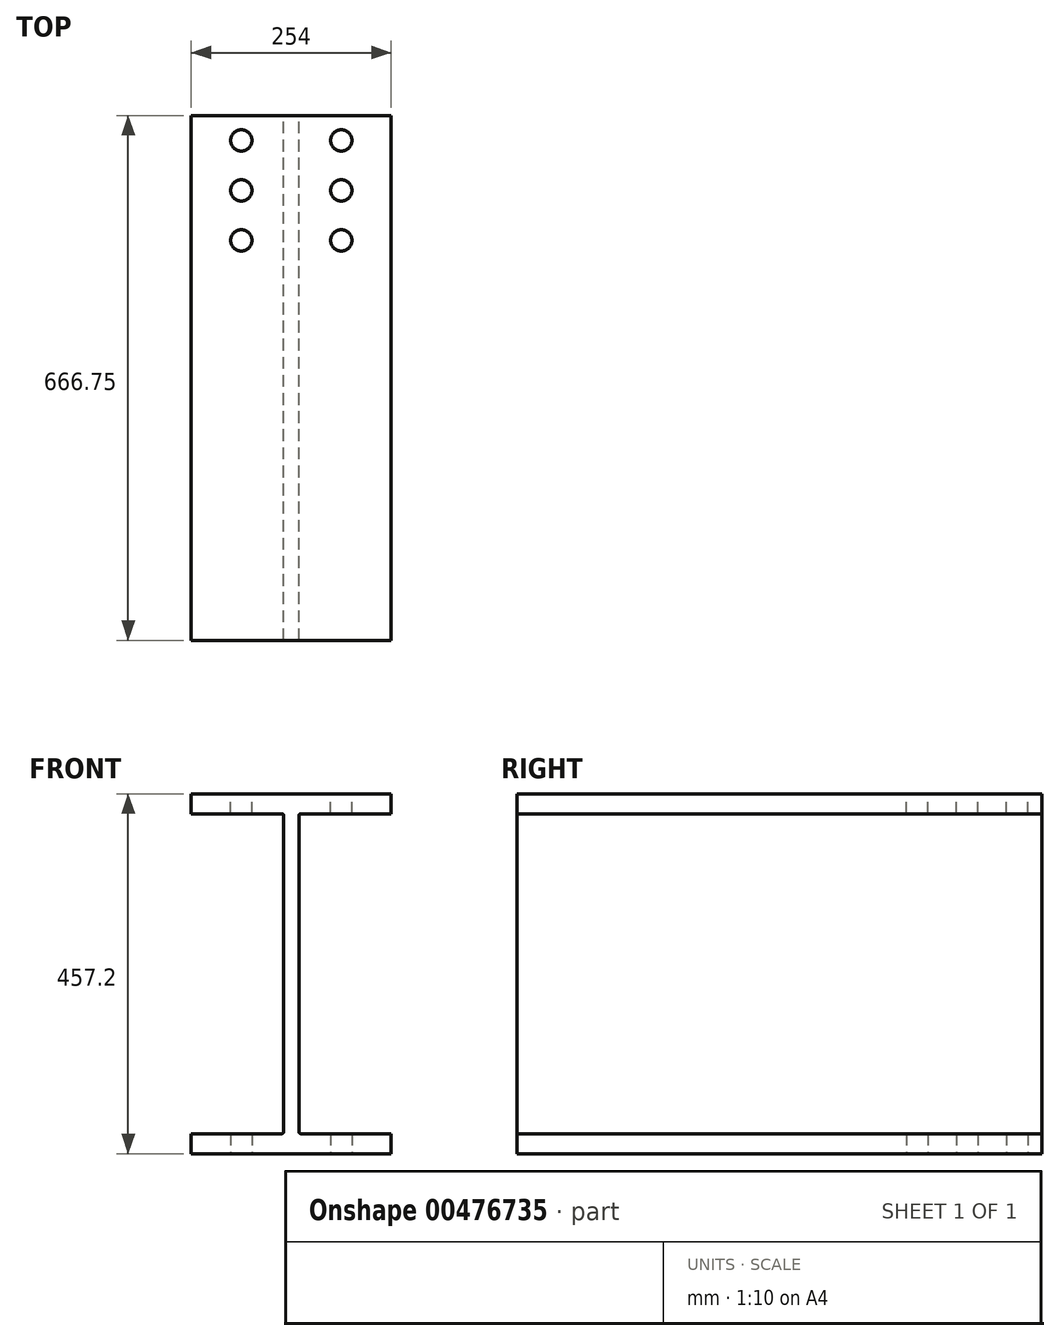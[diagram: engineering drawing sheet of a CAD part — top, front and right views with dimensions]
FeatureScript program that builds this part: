
annotation { "Feature Type Name" : "Feature", "Feature Type Description" : "" }
export const myFeature = defineFeature(function(context is Context, id is Id, definition is map)
    precondition{}
    {
        {
            var Q0;
            Q0=qCreatedBy(makeId("Front.planeOp"),FACE);
            var sketch = newSketch(context, id + "F0", { "sketchPlane" : qUnion([Q0])});
            skLineSegment(sketch, "E0", {"start": v(127, -203.2) * mm, "end": v(12.06, -203.2) * mm});
            skLineSegment(sketch, "E1", {"start": v(9.52, -200.66) * mm, "end": v(9.52, 200.66) * mm});
            skLineSegment(sketch, "E2", {"start": v(12.06, 203.2) * mm, "end": v(127, 203.2) * mm});
            skLineSegment(sketch, "E3", {"start": v(-127, 203.2) * mm, "end": v(-12.06, 203.2) * mm});
            skLineSegment(sketch, "E4", {"start": v(-9.53, 200.66) * mm, "end": v(-9.53, -200.66) * mm});
            skLineSegment(sketch, "E5", {"start": v(-12.06, -203.2) * mm, "end": v(-127, -203.2) * mm});
            skLineSegment(sketch, "E6", {"start": v(0, 0) * mm, "end": v(-9.52, 0) * mm, "construction": true});
            skLineSegment(sketch, "E7", {"start": v(0, 0) * mm, "end": v(9.52, 0) * mm, "construction": true});
            skLineSegment(sketch, "E8", {"start": v(0, 0) * mm, "end": v(0, 228.6) * mm, "construction": true});
            skLineSegment(sketch, "E9", {"start": v(0, 0) * mm, "end": v(0, -228.6) * mm, "construction": true});
            skPoint(sketch, "E10.visualSharp", {"position": v(-9.53, 203.2) * mm});
            skArc(sketch, "E10.filletArc", {"start": v(-9.52, 200.66) * mm, "mid": v(-10.27, 202.46) * mm, "end": v(-12.06, 203.2) * mm});
            skPoint(sketch, "E11.visualSharp", {"position": v(9.53, 203.2) * mm});
            skArc(sketch, "E11.filletArc", {"start": v(12.06, 203.2) * mm, "mid": v(10.27, 202.46) * mm, "end": v(9.52, 200.66) * mm});
            skPoint(sketch, "E12.visualSharp", {"position": v(9.53, -203.2) * mm});
            skArc(sketch, "E12.filletArc", {"start": v(9.52, -200.66) * mm, "mid": v(10.27, -202.46) * mm, "end": v(12.06, -203.2) * mm});
            skPoint(sketch, "E13.visualSharp", {"position": v(-9.53, -203.2) * mm});
            skArc(sketch, "E13.filletArc", {"start": v(-12.06, -203.2) * mm, "mid": v(-10.27, -202.46) * mm, "end": v(-9.52, -200.66) * mm});
            skPoint(sketch, "E14.visualSharp", {"position": v(-127, 228.6) * mm});
            skPoint(sketch, "E15.visualSharp", {"position": v(127, 228.6) * mm});
            skPoint(sketch, "E16.visualSharp", {"position": v(127, 203.2) * mm});
            skPoint(sketch, "E17.visualSharp", {"position": v(127, -228.6) * mm});
            skPoint(sketch, "E18.visualSharp", {"position": v(-127, -203.2) * mm});
            skPoint(sketch, "E19.visualSharp", {"position": v(-127, -228.6) * mm});
            skLineSegment(sketch, "E20", {"start": v(127, -203.2) * mm, "end": v(127, -228.6) * mm});
            skLineSegment(sketch, "E21", {"start": v(-127, -203.2) * mm, "end": v(-127, -228.6) * mm});
            skLineSegment(sketch, "E22", {"start": v(-127, 228.6) * mm, "end": v(-127, 203.2) * mm});
            skLineSegment(sketch, "E23", {"start": v(127, 228.6) * mm, "end": v(127, 203.2) * mm});
            skLineSegment(sketch, "E24", {"start": v(-127, 228.6) * mm, "end": v(127, 228.6) * mm});
            skLineSegment(sketch, "E25", {"start": v(-127, -228.6) * mm, "end": v(127, -228.6) * mm});
            skSolve(sketch);
        }
        {
            var Q0;
            Q0=makeQuery(id+"F0.imprint","IMPRINT",FACE,{"disambiguationData":[TD([[makeQuery(id+"F0.imprint","IMPRINT",EDGE,{"derivedFrom":sQuery(id+"F0.wireOp",EDGE,"E0")}),1.0]])]});
            extrude(context, id + "F1", {"entities" : qUnion([Q0]), "depth" : 508 * mm, "hasSecondDirection" : true, "secondDirectionOppositeDirection" : true, "secondDirectionDepth" : 158.75 * mm});
        }
        {
            var Q0;
            Q0=makeQuery(id+"F1.opExtrude","SWEPT_FACE",FACE,{"disambiguationData":[OSD([sQuery(id+"F0.wireOp",EDGE,"E24")])]});
            var sketch = newSketch(context, id + "F2", { "sketchPlane" : qUnion([Q0])});
            skLineSegment(sketch, "E26", {"start": v(0, 470.86) * mm, "end": v(0, -382.8) * mm, "construction": true});
            skPoint(sketch, "E27", {"position": v(63.5, 127) * mm});
            skPoint(sketch, "E28.0.1.0", {"position": v(63.5, 63.5) * mm});
            skPoint(sketch, "E28.0.2.0", {"position": v(63.5, 0) * mm});
            skLineSegment(sketch, "E28.direction1", {"start": v(63.5, 127) * mm, "end": v(88.9, 127) * mm, "construction": true});
            skLineSegment(sketch, "E28.direction2", {"start": v(63.5, 127) * mm, "end": v(63.5, 63.5) * mm, "construction": true});
            skPoint(sketch, "E29.MirrorP", {"position": v(-63.5, 0) * mm});
            skLineSegment(sketch, "E30.MirrorCS", {"start": v(-63.5, 127) * mm, "end": v(-63.5, 63.5) * mm, "construction": true});
            skPoint(sketch, "E31.MirrorP", {"position": v(-63.5, 127) * mm});
            skPoint(sketch, "E32.MirrorP", {"position": v(-63.5, 63.5) * mm});
            skSolve(sketch);
        }
        {
            var Q0;
            Q0=sQuery(id+"F2.wireOp",VERTEX,"E27");
            var Q1;
            Q1=sQuery(id+"F2.wireOp",VERTEX,"E28.0.1.0");
            var Q2;
            Q2=sQuery(id+"F2.wireOp",VERTEX,"E28.0.2.0");
            var Q3;
            Q3=sQuery(id+"F2.wireOp",VERTEX,"E28.0.3.0");
            var Q4;
            Q4=sQuery(id+"F2.wireOp",VERTEX,"E28.0.4.0");
            var Q5;
            Q5=sQuery(id+"F2.wireOp",VERTEX,"E28.0.5.0");
            var Q6;
            Q6=sQuery(id+"F2.wireOp",VERTEX,"10dad2e2-d4e5-4773-874c-b5d4de7557793.MirrorP");
            var Q7;
            Q7=sQuery(id+"F2.wireOp",VERTEX,"10dad2e2-d4e5-4773-874c-b5d4de7557794.MirrorP");
            var Q8;
            Q8=sQuery(id+"F2.wireOp",VERTEX,"10dad2e2-d4e5-4773-874c-b5d4de7557795.MirrorP");
            var Q9;
            Q9=sQuery(id+"F2.wireOp",VERTEX,"E29.MirrorP");
            var Q10;
            Q10=sQuery(id+"F2.wireOp",VERTEX,"E30.MirrorCS.end");
            var Q11;
            Q11=sQuery(id+"F2.wireOp",VERTEX,"E31.MirrorP");
            var Q12;
            Q12=makeQuery(id+"F1.opExtrude","SWEPT_BODY",BODY,{"disambiguationData":[OSD([sQuery(id+"F0.wireOp",EDGE,"E0"),sQuery(id+"F0.wireOp",EDGE,"E1"),sQuery(id+"F0.wireOp",EDGE,"E2"),sQuery(id+"F0.wireOp",EDGE,"E3"),sQuery(id+"F0.wireOp",EDGE,"E4"),sQuery(id+"F0.wireOp",EDGE,"E5"),sQuery(id+"F0.wireOp",EDGE,"E10.filletArc"),sQuery(id+"F0.wireOp",EDGE,"E11.filletArc"),sQuery(id+"F0.wireOp",EDGE,"E12.filletArc"),sQuery(id+"F0.wireOp",EDGE,"E13.filletArc"),sQuery(id+"F0.wireOp",EDGE,"E20"),sQuery(id+"F0.wireOp",EDGE,"E21"),sQuery(id+"F0.wireOp",EDGE,"E22"),sQuery(id+"F0.wireOp",EDGE,"E23"),sQuery(id+"F0.wireOp",EDGE,"E24"),sQuery(id+"F0.wireOp",EDGE,"E25")])]});
            hole(context, id + "F3", {"style" : HoleStyle.SIMPLE, "endStyle" : HoleEndStyle.BLIND, "holeDiameter" : 26.99 * mm, "holeDepth" : 25.4 * mm, "isTappedThrough" : true, "tappedDepth" : 12.7 * mm, "tapClearance" : 3, "locations" : qUnion([Q0, Q1, Q2, Q3, Q4, Q5, Q6, Q7, Q8, Q9, Q10, Q11]), "scope" : qUnion([Q12])});
        }
        {
            var Q0;
            Q0=makeQuery(id+"F1.opExtrude","SWEPT_FACE",FACE,{"disambiguationData":[OSD([sQuery(id+"F0.wireOp",EDGE,"E25")])]});
            var sketch = newSketch(context, id + "F4", { "sketchPlane" : qUnion([Q0])});
            skLineSegment(sketch, "E33", {"start": v(0, 396.6) * mm, "end": v(0, -457.05) * mm, "construction": true});
            skPoint(sketch, "E34", {"position": v(63.5, 0) * mm});
            skPoint(sketch, "E35.0.1.0", {"position": v(63.5, -63.5) * mm});
            skPoint(sketch, "E35.0.2.0", {"position": v(63.5, -127) * mm});
            skLineSegment(sketch, "E35.direction1", {"start": v(63.5, 0) * mm, "end": v(88.9, 0) * mm, "construction": true});
            skLineSegment(sketch, "E35.direction2", {"start": v(63.5, 0) * mm, "end": v(63.5, -63.5) * mm, "construction": true});
            skPoint(sketch, "E36.MirrorP", {"position": v(-63.5, -127) * mm});
            skLineSegment(sketch, "E37.MirrorCS", {"start": v(-63.5, 0) * mm, "end": v(-63.5, -63.5) * mm, "construction": true});
            skPoint(sketch, "E38.MirrorP", {"position": v(-63.5, 0) * mm});
            skPoint(sketch, "E39.MirrorP", {"position": v(-63.5, -63.5) * mm});
            skSolve(sketch);
        }
        {
            var Q0;
            Q0=sQuery(id+"F4.wireOp",VERTEX,"E35.0.2.0");
            var Q1;
            Q1=sQuery(id+"F4.wireOp",VERTEX,"E35.0.1.0");
            var Q2;
            Q2=sQuery(id+"F4.wireOp",VERTEX,"E34");
            var Q3;
            Q3=sQuery(id+"F4.wireOp",VERTEX,"E38.MirrorP");
            var Q4;
            Q4=sQuery(id+"F4.wireOp",VERTEX,"E39.MirrorP");
            var Q5;
            Q5=sQuery(id+"F4.wireOp",VERTEX,"E36.MirrorP");
            var Q6;
            Q6=makeQuery(id+"F1.opExtrude","SWEPT_BODY",BODY,{"disambiguationData":[OSD([sQuery(id+"F0.wireOp",EDGE,"E0"),sQuery(id+"F0.wireOp",EDGE,"E1"),sQuery(id+"F0.wireOp",EDGE,"E2"),sQuery(id+"F0.wireOp",EDGE,"E3"),sQuery(id+"F0.wireOp",EDGE,"E4"),sQuery(id+"F0.wireOp",EDGE,"E5"),sQuery(id+"F0.wireOp",EDGE,"E10.filletArc"),sQuery(id+"F0.wireOp",EDGE,"E11.filletArc"),sQuery(id+"F0.wireOp",EDGE,"E12.filletArc"),sQuery(id+"F0.wireOp",EDGE,"E13.filletArc"),sQuery(id+"F0.wireOp",EDGE,"E20"),sQuery(id+"F0.wireOp",EDGE,"E21"),sQuery(id+"F0.wireOp",EDGE,"E22"),sQuery(id+"F0.wireOp",EDGE,"E23"),sQuery(id+"F0.wireOp",EDGE,"E24"),sQuery(id+"F0.wireOp",EDGE,"E25")])]});
            hole(context, id + "F5", {"style" : HoleStyle.SIMPLE, "endStyle" : HoleEndStyle.BLIND, "holeDiameter" : 26.99 * mm, "holeDepth" : 25.4 * mm, "isTappedThrough" : true, "tappedDepth" : 12.7 * mm, "tapClearance" : 3, "locations" : qUnion([Q0, Q1, Q2, Q3, Q4, Q5]), "scope" : qUnion([Q6])});
        }
    });
